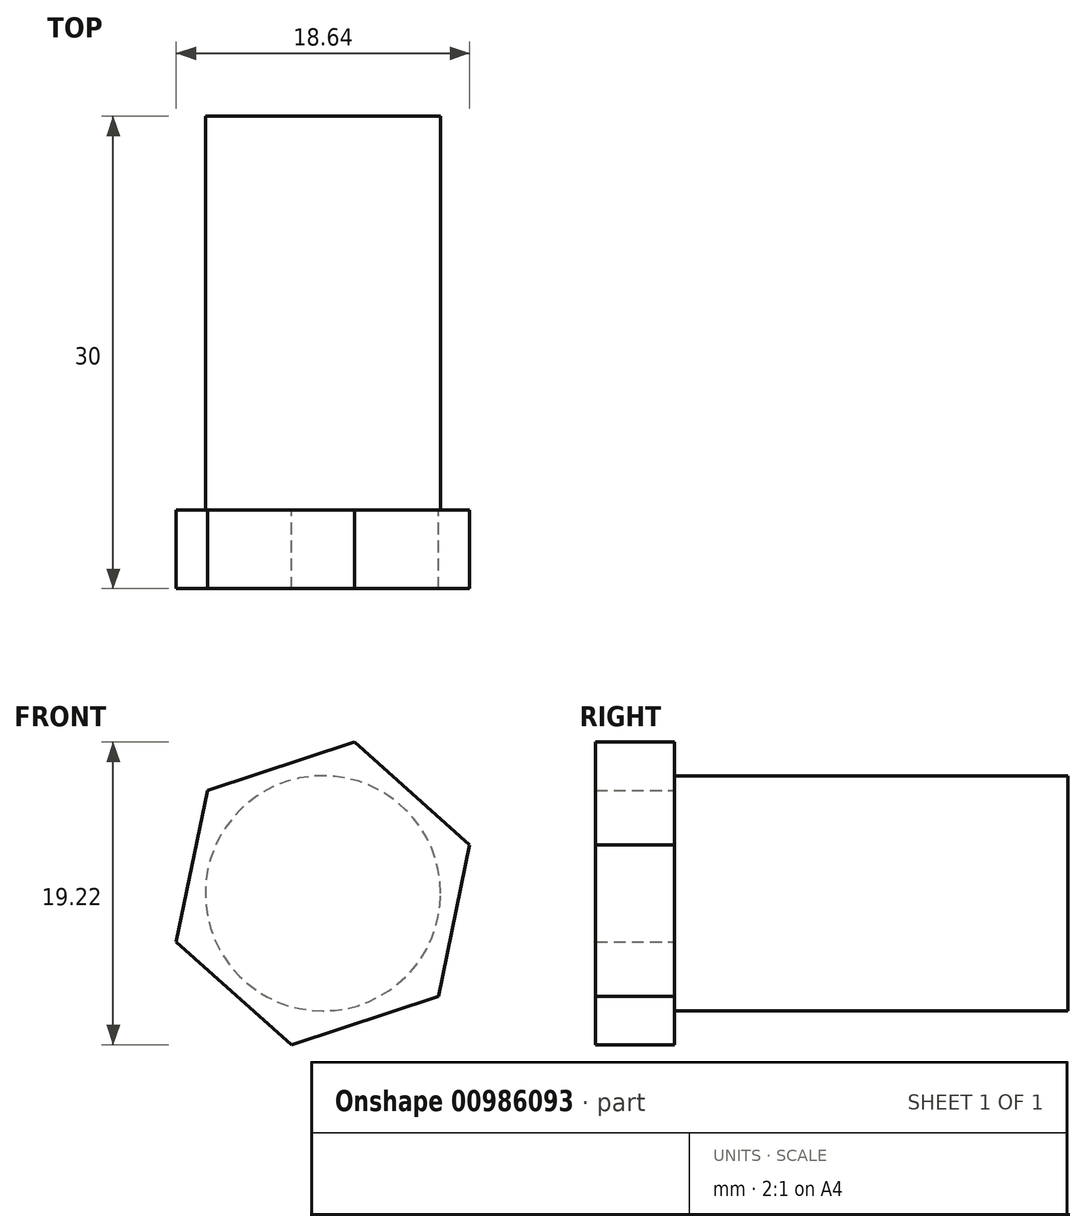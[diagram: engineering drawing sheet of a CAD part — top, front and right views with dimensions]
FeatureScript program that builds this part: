
annotation { "Feature Type Name" : "Feature", "Feature Type Description" : "" }
export const myFeature = defineFeature(function(context is Context, id is Id, definition is map)
    precondition{}
    {
        {
            var Q0;
            Q0=qCreatedBy(makeId("Front.planeOp"),FACE);
            var sketch = newSketch(context, id + "F0", { "sketchPlane" : qUnion([Q0])});
            skCircle(sketch, "E0.cCircle", {"center": v(0, 0) * mm, "radius": 8.5 * mm, "construction": true});
            skLineSegment(sketch, "E0.0", {"start": v(2, 9.61) * mm, "end": v(9.32, 3.08) * mm});
            skLineSegment(sketch, "E0.1", {"start": v(9.32, 3.08) * mm, "end": v(7.33, -6.53) * mm});
            skLineSegment(sketch, "E0.2", {"start": v(7.33, -6.53) * mm, "end": v(-2, -9.61) * mm});
            skLineSegment(sketch, "E0.3", {"start": v(-2, -9.61) * mm, "end": v(-9.32, -3.08) * mm});
            skLineSegment(sketch, "E0.4", {"start": v(-9.32, -3.08) * mm, "end": v(-7.33, 6.53) * mm});
            skLineSegment(sketch, "E0.5", {"start": v(-7.33, 6.53) * mm, "end": v(2, 9.61) * mm});
            skPoint(sketch, "E0.0.midPoint", {"position": v(5.65, 6.35) * mm});
            skSolve(sketch);
        }
        {
            var Q0;
            Q0=makeQuery(id+"F0.imprint","IMPRINT",FACE,{"disambiguationData":[TD([[makeQuery(id+"F0.imprint","IMPRINT",EDGE,{"derivedFrom":sQuery(id+"F0.wireOp",EDGE,"E0.0")}),-1.0]])]});
            extrude(context, id + "F1", {"entities" : qUnion([Q0]), "depth" : 5 * mm, "offsetDistance" : 25 * mm});
        }
        {
            var Q0;
            Q0=makeQuery(id+"F1.opExtrude","CAP_FACE",FACE,{"disambiguationData":[OSD([sQuery(id+"F0.wireOp",EDGE,"E0.0"),sQuery(id+"F0.wireOp",EDGE,"E0.1"),sQuery(id+"F0.wireOp",EDGE,"E0.2"),sQuery(id+"F0.wireOp",EDGE,"E0.3"),sQuery(id+"F0.wireOp",EDGE,"E0.4"),sQuery(id+"F0.wireOp",EDGE,"E0.5")])],"isStart":true});
            var sketch = newSketch(context, id + "F2", { "sketchPlane" : qUnion([Q0])});
            skCircle(sketch, "E1", {"center": v(0, 0) * mm, "radius": 7.47 * mm});
            skSolve(sketch);
        }
        {
            var Q0;
            Q0=qSketchRegion(id+"F2",true);
            extrude(context, id + "F3", {"entities" : qUnion([Q0]), "operationType" : NewBodyOperationType.ADD, "depth" : 25 * mm, "offsetDistance" : 25 * mm});
        }
    });
